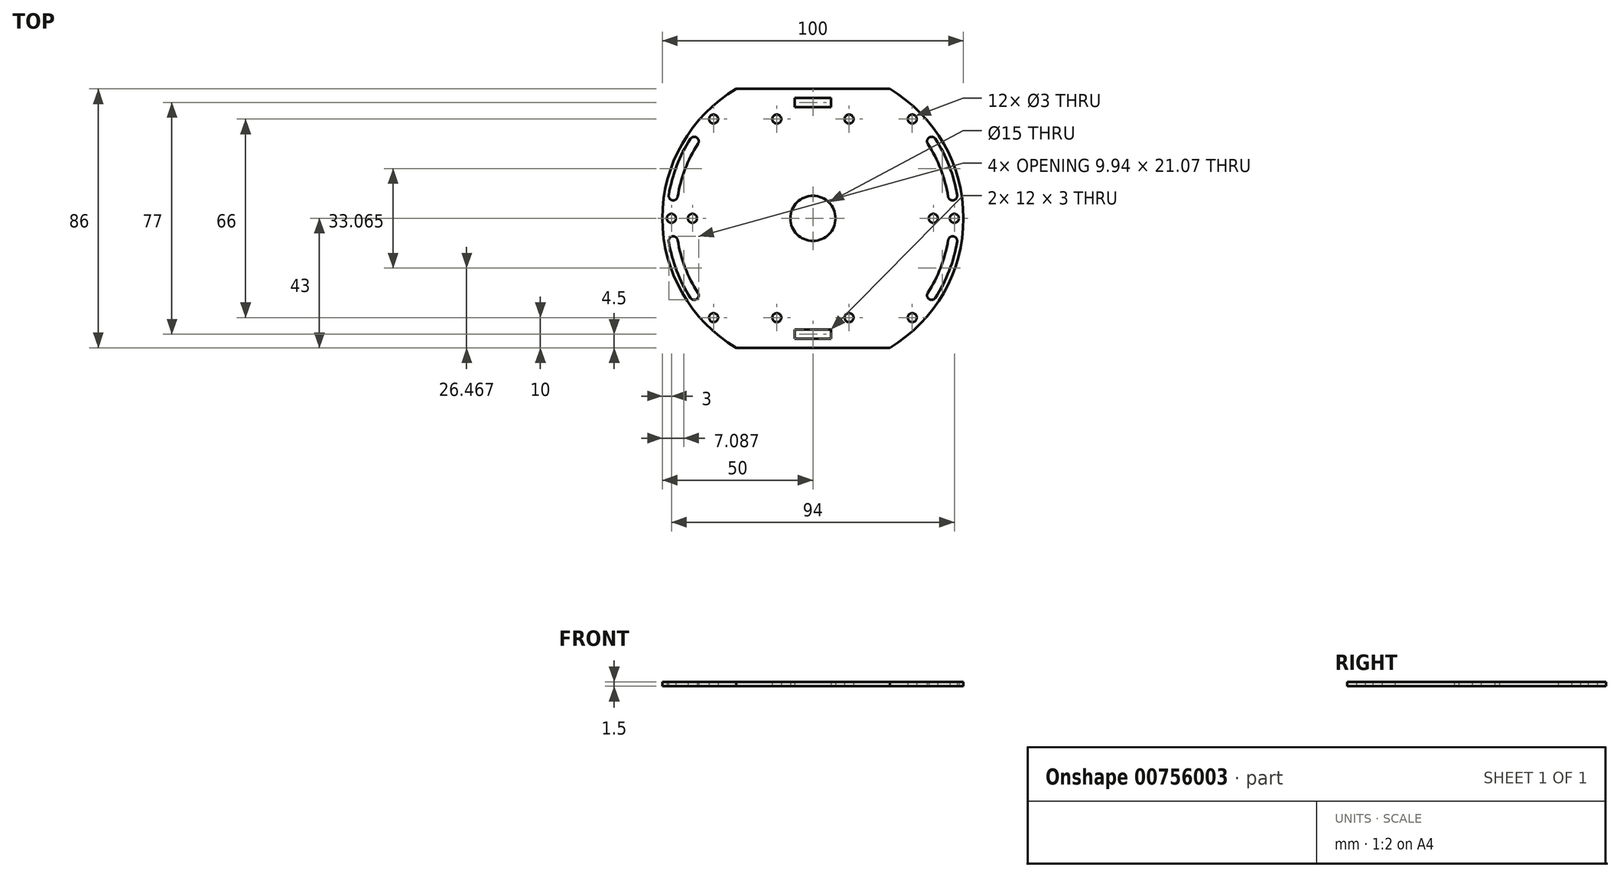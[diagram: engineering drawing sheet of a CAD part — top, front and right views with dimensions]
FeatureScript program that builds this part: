
annotation { "Feature Type Name" : "Feature", "Feature Type Description" : "" }
export const myFeature = defineFeature(function(context is Context, id is Id, definition is map)
    precondition{}
    {
        {
            var Q0;
            Q0=qCreatedBy(makeId("Top.planeOp"),FACE);
            var sketch = newSketch(context, id + "F0", { "sketchPlane" : qUnion([Q0])});
            skArc(sketch, "E0", {"start": v(-25.51, 43) * mm, "mid": v(-50, 0) * mm, "end": v(-25.51, -43) * mm});
            skLineSegment(sketch, "E1", {"start": v(-25.51, 43) * mm, "end": v(25.51, 43) * mm});
            skLineSegment(sketch, "E2", {"start": v(-25.51, -43) * mm, "end": v(25.51, -43) * mm});
            skLineSegment(sketch, "E3", {"start": v(0, 43) * mm, "end": v(0, 0) * mm, "construction": true});
            skLineSegment(sketch, "E4", {"start": v(0, 0) * mm, "end": v(0, -43) * mm, "construction": true});
            skArc(sketch, "E5.trimOffspring", {"start": v(25.51, -43) * mm, "mid": v(50, 0) * mm, "end": v(25.51, 43) * mm});
            skCircle(sketch, "E6", {"center": v(0, 0) * mm, "radius": 7.5 * mm});
            skLineSegment(sketch, "E7", {"start": v(-50, 0) * mm, "end": v(50, 0) * mm, "construction": true});
            skCircle(sketch, "E8", {"center": v(-47, 0) * mm, "radius": 1.5 * mm});
            skCircle(sketch, "E9", {"center": v(47, 0) * mm, "radius": 1.5 * mm});
            skLineSegment(sketch, "E10", {"start": v(-37.56, 33) * mm, "end": v(37.56, 33) * mm, "construction": true});
            skCircle(sketch, "E11", {"center": v(-12, 33) * mm, "radius": 1.5 * mm});
            skCircle(sketch, "E12", {"center": v(-33, 33) * mm, "radius": 1.5 * mm});
            skCircle(sketch, "E13.MirrorC", {"center": v(-12, -33) * mm, "radius": 1.5 * mm});
            skCircle(sketch, "E14.MirrorC", {"center": v(-33, -33) * mm, "radius": 1.5 * mm});
            skCircle(sketch, "E15.MirrorC", {"center": v(12, -33) * mm, "radius": 1.5 * mm});
            skCircle(sketch, "E16.MirrorC", {"center": v(33, -33) * mm, "radius": 1.5 * mm});
            skCircle(sketch, "E17.MirrorC", {"center": v(12, 33) * mm, "radius": 1.5 * mm});
            skCircle(sketch, "E18.MirrorC", {"center": v(33, 33) * mm, "radius": 1.5 * mm});
            skArc(sketch, "E19", {"start": v(-47.88, 7.71) * mm, "mid": v(-45.26, 17.44) * mm, "end": v(-40.68, 26.41) * mm});
            skArc(sketch, "E20", {"start": v(-44.92, 7.24) * mm, "mid": v(-42.46, 16.36) * mm, "end": v(-38.16, 24.78) * mm});
            skArc(sketch, "E21", {"start": v(-47.88, 7.71) * mm, "mid": v(-46.64, 6) * mm, "end": v(-44.92, 7.24) * mm});
            skPoint(sketch, "E21.third.point", {"position": v(-45.92, 6.05) * mm});
            skArc(sketch, "E22", {"start": v(-38.16, 24.78) * mm, "mid": v(-38.6, 26.85) * mm, "end": v(-40.68, 26.41) * mm});
            skPoint(sketch, "E22.third.point", {"position": v(-40.3, 24.38) * mm});
            skArc(sketch, "E23.MirrorC", {"start": v(47.88, 7.71) * mm, "mid": v(46.64, 6) * mm, "end": v(44.92, 7.24) * mm});
            skArc(sketch, "E24.MirrorC", {"start": v(38.16, 24.78) * mm, "mid": v(38.6, 26.85) * mm, "end": v(40.68, 26.41) * mm});
            skArc(sketch, "E25.MirrorCS", {"start": v(47.88, 7.71) * mm, "mid": v(45.26, 17.44) * mm, "end": v(40.68, 26.41) * mm});
            skArc(sketch, "E26.MirrorCS", {"start": v(44.92, 7.24) * mm, "mid": v(42.46, 16.36) * mm, "end": v(38.16, 24.78) * mm});
            skArc(sketch, "E27.MirrorCS", {"start": v(-47.88, -7.71) * mm, "mid": v(-45.26, -17.44) * mm, "end": v(-40.68, -26.41) * mm});
            skArc(sketch, "E28.MirrorCS", {"start": v(-44.92, -7.24) * mm, "mid": v(-42.46, -16.36) * mm, "end": v(-38.16, -24.78) * mm});
            skArc(sketch, "E29.MirrorC", {"start": v(-38.16, -24.78) * mm, "mid": v(-38.6, -26.85) * mm, "end": v(-40.68, -26.41) * mm});
            skArc(sketch, "E30.MirrorC", {"start": v(-47.88, -7.71) * mm, "mid": v(-46.64, -6) * mm, "end": v(-44.92, -7.24) * mm});
            skArc(sketch, "E31.MirrorC", {"start": v(38.16, -24.78) * mm, "mid": v(38.6, -26.85) * mm, "end": v(40.68, -26.41) * mm});
            skArc(sketch, "E32.MirrorCS", {"start": v(44.92, -7.24) * mm, "mid": v(42.46, -16.36) * mm, "end": v(38.16, -24.78) * mm});
            skArc(sketch, "E33.MirrorCS", {"start": v(47.88, -7.71) * mm, "mid": v(45.26, -17.44) * mm, "end": v(40.68, -26.41) * mm});
            skArc(sketch, "E34.MirrorC", {"start": v(47.88, -7.71) * mm, "mid": v(46.64, -6) * mm, "end": v(44.92, -7.24) * mm});
            skLineSegment(sketch, "E35.bottom", {"start": v(6, 40) * mm, "end": v(-6, 40) * mm});
            skLineSegment(sketch, "E35.top", {"start": v(6, 37) * mm, "end": v(-6, 37) * mm});
            skLineSegment(sketch, "E35.left", {"start": v(6, 40) * mm, "end": v(6, 37) * mm});
            skLineSegment(sketch, "E35.right", {"start": v(-6, 40) * mm, "end": v(-6, 37) * mm});
            skPoint(sketch, "E35.middle", {"position": v(0, 38.5) * mm});
            skLineSegment(sketch, "E36.MirrorCS", {"start": v(6, -40) * mm, "end": v(-6, -40) * mm});
            skLineSegment(sketch, "E37.MirrorCS", {"start": v(-6, -40) * mm, "end": v(-6, -37) * mm});
            skLineSegment(sketch, "E38.MirrorCS", {"start": v(6, -37) * mm, "end": v(-6, -37) * mm});
            skLineSegment(sketch, "E39.MirrorCS", {"start": v(6, -40) * mm, "end": v(6, -37) * mm});
            skCircle(sketch, "E40", {"center": v(-40, 0) * mm, "radius": 1.5 * mm});
            skCircle(sketch, "E41.MirrorC", {"center": v(40, 0) * mm, "radius": 1.5 * mm});
            skArc(sketch, "E42", {"start": v(-39.42, -25.6) * mm, "mid": v(-43.86, -16.9) * mm, "end": v(-46.4, -7.48) * mm, "construction": true});
            skSolve(sketch);
        }
        {
            var Q0;
            Q0=makeQuery(id+"F0.imprint","IMPRINT",FACE,{"disambiguationData":[TD([[makeQuery(id+"F0.imprint","IMPRINT",EDGE,{"derivedFrom":sQuery(id+"F0.wireOp",EDGE,"E0")}),1.0]])]});
            extrude(context, id + "F1", {"entities" : qUnion([Q0]), "depth" : 1.5 * mm, "offsetDistance" : 25 * mm});
        }
    });
